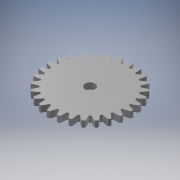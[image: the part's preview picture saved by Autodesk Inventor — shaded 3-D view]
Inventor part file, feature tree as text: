
AUTODESK INVENTOR PART (.ipt)
format: ipt  version: 2017 (Build 210142000, 142)  size: 266,752 bytes
history: native  units: mm (DEFAULTED — no unit token found)
features: sketch x4, extrude x3, plane x3, other x3
ambient origin geometry x8: Origin, YZ Plane, XZ Plane, XY Plane, X Axis, Y Axis, Z Axis, Center Point
bodies: Solid1 (feature_tree)
feature tree (13):
  extrude  "Extrusion1"  Depth=5.0mm TaperAngle=0.0deg
  plane  "Work Plane2"
  plane  "Work Plane8"
  plane  "Work Plane9"
  other  "Spur Gear"
  extrude  "Extrusion2"  Depth=10.0mm TaperAngle=0.0deg
  extrude  "Extrusion3"  Depth=1.121997mm TaperAngle=0.0deg
  sketch  "Sketch1"  dims[d0=67.5mm d1=5.0mm d2=0.0mm]
  sketch  "Sketch2"  dims[d3=63.0mm d4=10.0mm d5=0.0mm]
  other  "Srf1"
  sketch  "Sketch3"  dims[d16=63.0mm d17=0.0mm d34=1.121997mm]
  sketch  "Sketch4"  dims[d39=0.0mm d41=0.0mm d43=63.0mm d46=63.0mm d47=0.0mm d48=0.0mm d49=8.0mm d50=10.0mm d51=0.0mm d52=20.0mm d53=20.0mm d54=3.4mm d55=10.0mm d56=0.0mm]
  other  "Pitch Diameter"
